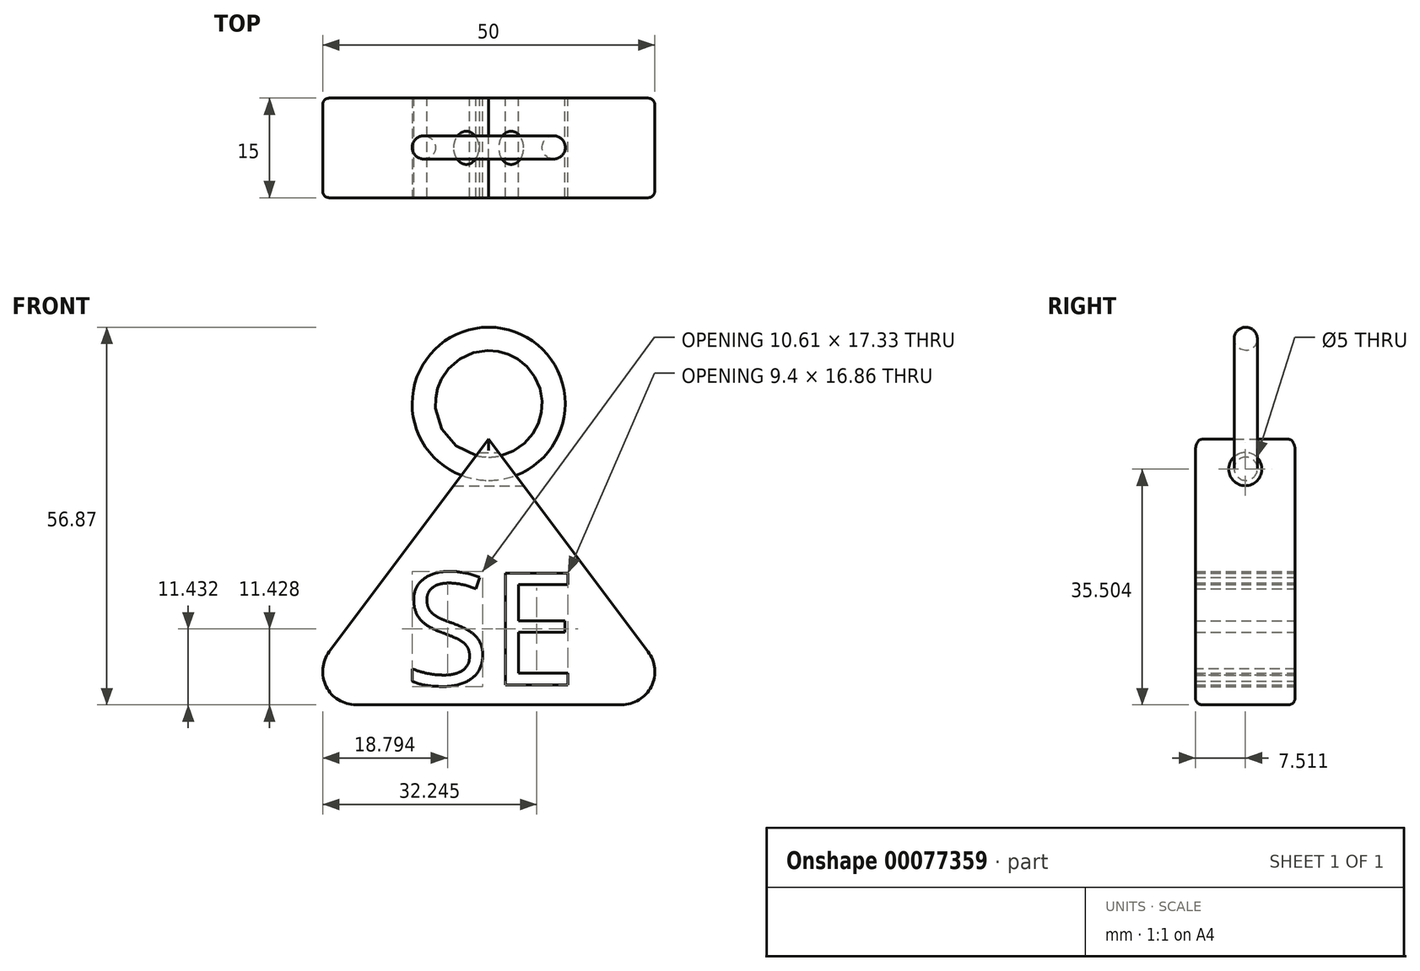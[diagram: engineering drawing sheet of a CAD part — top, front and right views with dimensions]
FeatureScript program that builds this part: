
annotation { "Feature Type Name" : "Feature", "Feature Type Description" : "" }
export const myFeature = defineFeature(function(context is Context, id is Id, definition is map)
    precondition{}
    {
        {
            var Q0;
            Q0=qCreatedBy(makeId("Front.planeOp"),FACE);
            var sketch = newSketch(context, id + "F0", { "sketchPlane" : qUnion([Q0])});
            skLineSegment(sketch, "E0", {"start": v(0, -5.34) * mm, "end": v(-30, -45.34) * mm});
            skLineSegment(sketch, "E1", {"start": v(-30, -45.34) * mm, "end": v(0, -45.34) * mm});
            skLineSegment(sketch, "E2.MirrorCS", {"start": v(0, -5.34) * mm, "end": v(30, -45.34) * mm});
            skLineSegment(sketch, "E3.MirrorCS", {"start": v(30, -45.34) * mm, "end": v(0, -45.34) * mm});
            skText(sketch, "E4", { "text": "SE", "fontName": "OpenSans-Regular.ttf"});
            skPoint(sketch, "E4.firstSnap0", {"position": v(-15, -25.34) * mm});
            const initialGuessF0  = {"E4": [-0.01273, -0.04234, 1, 0, 0.017]};
            skSetInitialGuess(sketch, initialGuessF0);
            skSolve(sketch);
        }
        {
            var Q0;
            Q0=makeQuery(id+"F0.imprint","IMPRINT",FACE,{"disambiguationData":[TD([[makeQuery(id+"F0.imprint","IMPRINT",EDGE,{"derivedFrom":sQuery(id+"F0.wireOp",EDGE,"E0")}),1.0]])]});
            extrude(context, id + "F1", {"entities" : qUnion([Q0]), "depth" : 15 * mm});
        }
        {
            var Q0;
            Q0=makeQuery(id+"F1.opExtrude","SWEPT_EDGE",EDGE,{"disambiguationData":[OSD([sQuery(id+"F0.wireOp",EDGE,"E2.MirrorCS"),sQuery(id+"F0.wireOp",EDGE,"E3.MirrorCS")])]});
            var Q1;
            Q1=makeQuery(id+"F1.opExtrude","SWEPT_EDGE",EDGE,{"disambiguationData":[OSD([sQuery(id+"F0.wireOp",EDGE,"E0"),sQuery(id+"F0.wireOp",EDGE,"E1")])]});
            fillet(context, id + "F2", {"entities" : qUnion([Q0, Q1]), "radius" : 5 * mm, "tangentPropagation" : true, "allowEdgeOverflow" : false});
        }
        {
            var Q0;
            Q0=makeQuery(id+"F2.opFillet","BLEND_FACE",FACE,{"disambiguationData":[OSD([sQuery(id+"F0.wireOp",EDGE,"E0"),sQuery(id+"F0.wireOp",EDGE,"E1")])]});
            var Q1;
            Q1=makeQuery(id+"F2.opFillet","BLEND_FACE",FACE,{"disambiguationData":[OSD([sQuery(id+"F0.wireOp",EDGE,"E2.MirrorCS"),sQuery(id+"F0.wireOp",EDGE,"E3.MirrorCS")])]});
            fillet(context, id + "F3", {"entities" : qUnion([Q0, Q1]), "radius" : 1 * mm, "tangentPropagation" : true, "allowEdgeOverflow" : false});
        }
        {
            var Q0;
            Q0=qCreatedBy(makeId("Right.planeOp"),FACE);
            var sketch = newSketch(context, id + "F4", { "sketchPlane" : qUnion([Q0])});
            skCircle(sketch, "E5", {"center": v(-7.49, -9.84) * mm, "radius": 2.5 * mm});
            skSolve(sketch);
        }
        {
            var Q0;
            Q0 = qSketchRegion(id + "F4", true);
            extrude(context, id + "F5", {"entities" : qUnion([Q0]), "operationType" : NewBodyOperationType.REMOVE, "endBound" : BoundingType.SYMMETRIC, "oppositeDirection" : true, "depth" : 25 * mm});
        }
        {
            var Q0;
            Q0=qCreatedBy(makeId("Right.planeOp"),FACE);
            var sketch = newSketch(context, id + "F6", { "sketchPlane" : qUnion([Q0])});
            skCircle(sketch, "E6", {"center": v(-7.43, -9.78) * mm, "radius": 1.75 * mm});
            skSolve(sketch);
        }
        {
            var Q0;
            Q0=qCreatedBy(makeId("Front.planeOp"),FACE);
            var Q1;
            Q1=sQuery(id+"F6.wireOp",VERTEX,"E6.center");
            cPlane(context, id + "F7", {"entities" : qUnion([Q0, Q1]), "cplaneType" : CPlaneType.PLANE_POINT, "offset" : 150 * mm, "width" : 150 * mm, "height" : 150 * mm});
        }
        {
            var Q0;
            Q0=qCreatedBy(id+"F7.planeOp",FACE);
            var sketch = newSketch(context, id + "F8", { "sketchPlane" : qUnion([Q0])});
            skCircle(sketch, "E7", {"center": v(0, 0) * mm, "radius": 10 * mm});
            skSolve(sketch);
        }
        {
            var Q0;
            Q0=makeQuery(id+"F6.imprint","IMPRINT",FACE,{"disambiguationData":[TD([[makeQuery(id+"F6.imprint","IMPRINT",EDGE,{"derivedFrom":sQuery(id+"F6.wireOp",EDGE,"E6")}),1.0]])]});
            var Q1;
            Q1=sQuery(id+"F8.wireOp",EDGE,"E7");
            sweep(context, id + "F9", {"profiles" : qUnion([Q0]), "path" : qUnion([Q1])});
        }
    });
